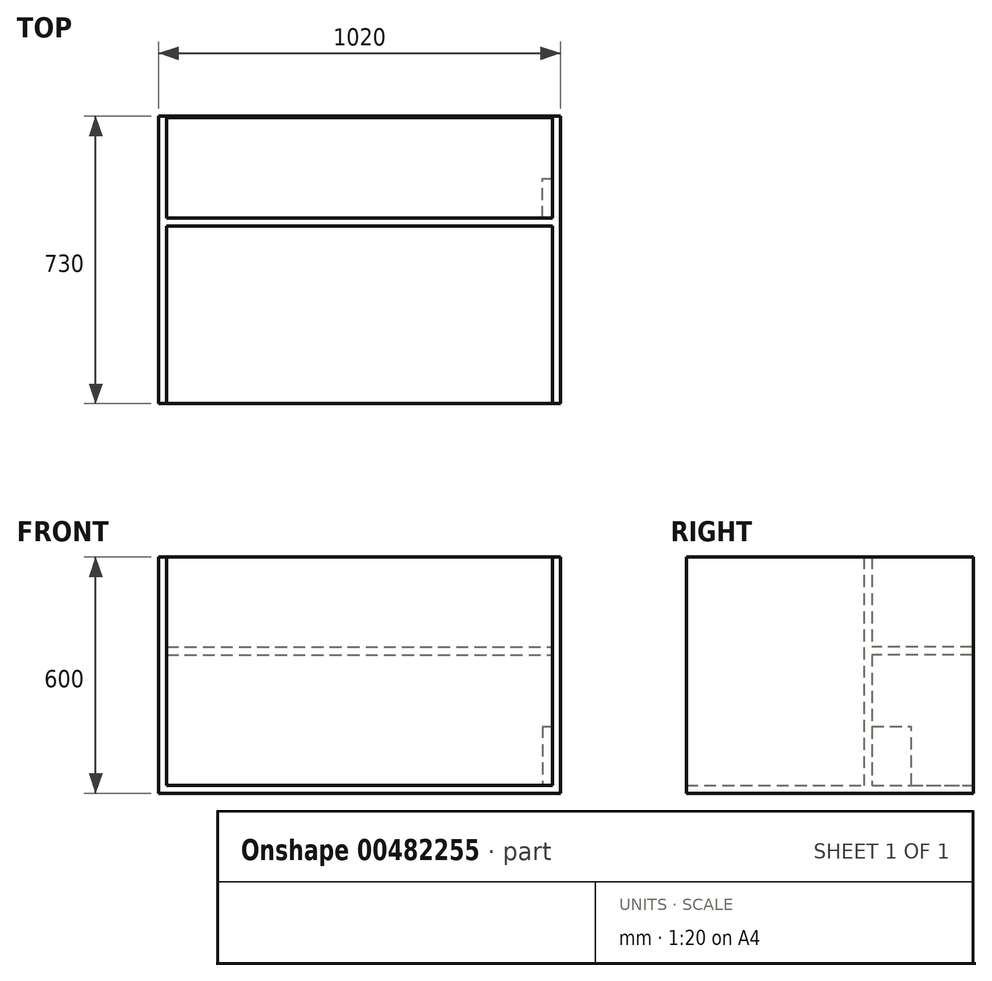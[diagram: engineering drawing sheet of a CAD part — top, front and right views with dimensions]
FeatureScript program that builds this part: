
annotation { "Feature Type Name" : "Feature", "Feature Type Description" : "" }
export const myFeature = defineFeature(function(context is Context, id is Id, definition is map)
    precondition{}
    {
        {
            var Q0;
            Q0=qCreatedBy(makeId("Top.planeOp"),FACE);
            var sketch = newSketch(context, id + "F0", { "sketchPlane" : qUnion([Q0])});
            skLineSegment(sketch, "E0.bottom", {"start": v(0, 0) * mm, "end": v(-1020, 0) * mm});
            skLineSegment(sketch, "E0.top", {"start": v(0, 730) * mm, "end": v(-1020, 730) * mm});
            skLineSegment(sketch, "E0.left", {"start": v(0, 0) * mm, "end": v(0, 730) * mm});
            skLineSegment(sketch, "E0.right", {"start": v(-1020, 0) * mm, "end": v(-1020, 730) * mm});
            skSolve(sketch);
        }
        {
            var Q0;
            Q0 = qSketchRegion(id + "F0", true);
            extrude(context, id + "F1", {"entities" : qUnion([Q0]), "depth" : 20 * mm});
        }
        {
            var Q0;
            Q0=makeQuery(id+"F1.opExtrude","CAP_FACE",FACE,{"disambiguationData":[OSD([sQuery(id+"F0.wireOp",EDGE,"E0.bottom"),sQuery(id+"F0.wireOp",EDGE,"E0.top"),sQuery(id+"F0.wireOp",EDGE,"E0.left"),sQuery(id+"F0.wireOp",EDGE,"E0.right")])],"isStart":false});
            var sketch = newSketch(context, id + "F2", { "sketchPlane" : qUnion([Q0])});
            skLineSegment(sketch, "E1.bottom", {"start": v(0, 0) * mm, "end": v(-20, 0) * mm});
            skLineSegment(sketch, "E1.top", {"start": v(0, 730) * mm, "end": v(-20, 730) * mm});
            skLineSegment(sketch, "E1.left", {"start": v(0, 0) * mm, "end": v(0, 730) * mm});
            skLineSegment(sketch, "E1.right", {"start": v(-20, 0) * mm, "end": v(-20, 730) * mm});
            skSolve(sketch);
        }
        {
            var Q0;
            Q0=makeQuery(id+"F2.imprint","IMPRINT",FACE,{"disambiguationData":[TD([[makeQuery(id+"F2.imprint","IMPRINT",EDGE,{"derivedFrom":sQuery(id+"F2.wireOp",EDGE,"E1.bottom")}),-1.0]])]});
            extrude(context, id + "F3", {"entities" : qUnion([Q0]), "operationType" : NewBodyOperationType.ADD, "depth" : 580 * mm});
        }
        {
            var Q0;
            Q0=makeQuery(id+"F1.opExtrude","CAP_FACE",FACE,{"disambiguationData":[OSD([sQuery(id+"F0.wireOp",EDGE,"E0.bottom"),sQuery(id+"F0.wireOp",EDGE,"E0.top"),sQuery(id+"F0.wireOp",EDGE,"E0.left"),sQuery(id+"F0.wireOp",EDGE,"E0.right")])],"isStart":false});
            var sketch = newSketch(context, id + "F4", { "sketchPlane" : qUnion([Q0])});
            skLineSegment(sketch, "E2.bottom", {"start": v(-1020, 0) * mm, "end": v(-1000, 0) * mm});
            skLineSegment(sketch, "E2.top", {"start": v(-1020, 730) * mm, "end": v(-1000, 730) * mm});
            skLineSegment(sketch, "E2.left", {"start": v(-1020, 0) * mm, "end": v(-1020, 730) * mm});
            skLineSegment(sketch, "E2.right", {"start": v(-1000, 0) * mm, "end": v(-1000, 730) * mm});
            skSolve(sketch);
        }
        {
            var Q0;
            Q0=makeQuery(id+"F4.imprint","IMPRINT",FACE,{"disambiguationData":[TD([[makeQuery(id+"F4.imprint","IMPRINT",EDGE,{"derivedFrom":sQuery(id+"F4.wireOp",EDGE,"E2.bottom")}),-1.0]])]});
            extrude(context, id + "F5", {"entities" : qUnion([Q0]), "operationType" : NewBodyOperationType.ADD, "depth" : 580 * mm});
        }
        {
            var Q0;
            Q0=makeQuery(id+"F1.opExtrude","CAP_FACE",FACE,{"disambiguationData":[OSD([sQuery(id+"F0.wireOp",EDGE,"E0.bottom"),sQuery(id+"F0.wireOp",EDGE,"E0.top"),sQuery(id+"F0.wireOp",EDGE,"E0.left"),sQuery(id+"F0.wireOp",EDGE,"E0.right")])],"isStart":false});
            var sketch = newSketch(context, id + "F6", { "sketchPlane" : qUnion([Q0])});
            skLineSegment(sketch, "E3.bottom", {"start": v(-1000, 471.58) * mm, "end": v(-20, 471.58) * mm});
            skLineSegment(sketch, "E3.top", {"start": v(-1000, 451.58) * mm, "end": v(-20, 451.58) * mm});
            skLineSegment(sketch, "E3.left", {"start": v(-1000, 471.58) * mm, "end": v(-1000, 451.58) * mm});
            skLineSegment(sketch, "E3.right", {"start": v(-20, 471.58) * mm, "end": v(-20, 451.58) * mm});
            skSolve(sketch);
        }
        {
            var Q0;
            Q0=makeQuery(id+"F6.imprint","IMPRINT",FACE,{"disambiguationData":[TD([[makeQuery(id+"F6.imprint","IMPRINT",EDGE,{"derivedFrom":sQuery(id+"F6.wireOp",EDGE,"E3.bottom")}),-1.0]])]});
            extrude(context, id + "F7", {"entities" : qUnion([Q0]), "operationType" : NewBodyOperationType.ADD, "depth" : 580 * mm});
        }
        {
            var Q0;
            Q0=makeQuery(id+"F7.opExtrude","SWEPT_FACE",FACE,{"disambiguationData":[OSD([sQuery(id+"F6.wireOp",EDGE,"E3.bottom")])]});
            var sketch = newSketch(context, id + "F8", { "sketchPlane" : qUnion([Q0])});
            skLineSegment(sketch, "E4.bottom", {"start": v(1000, 351.82) * mm, "end": v(20, 351.82) * mm});
            skLineSegment(sketch, "E4.top", {"start": v(1000, 371.82) * mm, "end": v(20, 371.82) * mm});
            skLineSegment(sketch, "E4.left", {"start": v(1000, 351.82) * mm, "end": v(1000, 371.82) * mm});
            skLineSegment(sketch, "E4.right", {"start": v(20, 351.82) * mm, "end": v(20, 371.82) * mm});
            skSolve(sketch);
        }
        {
            var Q0;
            Q0=makeQuery(id+"F8.imprint","IMPRINT",FACE,{"disambiguationData":[TD([[makeQuery(id+"F8.imprint","IMPRINT",EDGE,{"derivedFrom":sQuery(id+"F8.wireOp",EDGE,"E4.bottom")}),-1.0]])]});
            extrude(context, id + "F9", {"entities" : qUnion([Q0]), "operationType" : NewBodyOperationType.ADD, "depth" : 255 * mm});
        }
        {
            var Q0;
            {var subQ1=sQuery(id+"F2.wireOp",EDGE,"E1.right");var subQ2=sQuery(id+"F0.wireOp",EDGE,"E0.top");Q0=makeQuery(id+"F7.boolean.opBoolean","SPLIT",FACE,{"disambiguationData":[TD([makeQuery(id+"F1.opExtrude","SWEPT_FACE",FACE,{"disambiguationData":[OSD([subQ2])]})])],"derivedFrom":makeQuery(id+"F3.opExtrude","SWEPT_FACE",FACE,{"disambiguationData":[OSD([subQ1])]})});}
            var sketch = newSketch(context, id + "F10", { "sketchPlane" : qUnion([Q0])});
            skLineSegment(sketch, "E5.bottom", {"start": v(-471.58, 20) * mm, "end": v(-571.58, 20) * mm});
            skLineSegment(sketch, "E5.top", {"start": v(-471.58, 170) * mm, "end": v(-571.58, 170) * mm});
            skLineSegment(sketch, "E5.left", {"start": v(-471.58, 20) * mm, "end": v(-471.58, 170) * mm});
            skLineSegment(sketch, "E5.right", {"start": v(-571.58, 20) * mm, "end": v(-571.58, 170) * mm});
            skSolve(sketch);
        }
        {
            var Q0;
            Q0 = qSketchRegion(id + "F10", true);
            extrude(context, id + "F11", {"entities" : qUnion([Q0]), "operationType" : NewBodyOperationType.ADD, "depth" : 25 * mm});
        }
    });
